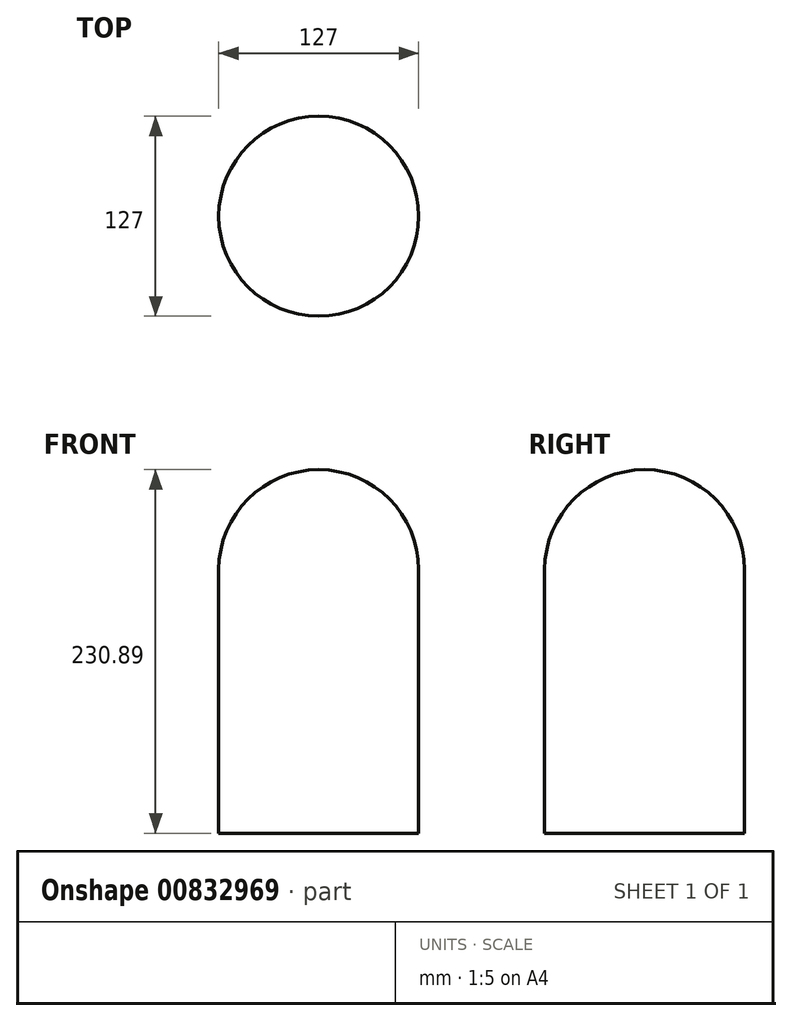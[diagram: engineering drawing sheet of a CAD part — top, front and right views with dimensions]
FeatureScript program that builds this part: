
annotation { "Feature Type Name" : "Feature", "Feature Type Description" : "" }
export const myFeature = defineFeature(function(context is Context, id is Id, definition is map)
    precondition{}
    {
        {
            var Q0;
            Q0=qCreatedBy(makeId("Top.planeOp"),FACE);
            var sketch = newSketch(context, id + "F0", { "sketchPlane" : qUnion([Q0])});
            skCircle(sketch, "E0", {"center": v(0, 0) * mm, "radius": 63.5 * mm});
            skSolve(sketch);
        }
        {
            var Q0;
            Q0 = qSketchRegion(id + "F0", true);
            extrude(context, id + "F1", {"entities" : qUnion([Q0]), "depth" : 167.39 * mm, "offsetDistance" : 25.4 * mm});
        }
        {
            var Q0;
            Q0=makeQuery(id+"F1.opExtrude","CAP_FACE",FACE,{"disambiguationData":[OSD([sQuery(id+"F0.wireOp",EDGE,"E0")])],"isStart":false});
            var sketch = newSketch(context, id + "F2", { "sketchPlane" : qUnion([Q0])});
            skLineSegment(sketch, "E1", {"start": v(0, 88.9) * mm, "end": v(0, -88.9) * mm});
            skArc(sketch, "E2", {"start": v(0, 88.9) * mm, "mid": v(88.9, 0) * mm, "end": v(0, -88.9) * mm});
            skSolve(sketch);
        }
        {
            var Q0;
            {var subQ0=sQuery(id+"F2.wireOp",EDGE,"E2");Q0=makeQuery(id+"F2.imprint","IMPRINT",FACE,{"disambiguationData":[TD([[makeQuery(id+"F2.imprint","IMPRINT",EDGE,{"derivedFrom":subQ0}),-1.0]])]});}
            var Q1;
            {var subQ0=sQuery(id+"F2.wireOp",EDGE,"E1");var subQ1=makeQuery(id+"F1.opExtrude","CAP_EDGE",EDGE,{"disambiguationData":[OSD([sQuery(id+"F0.wireOp",EDGE,"E0")])],"isStart":false});var subQ2=makeQuery(id+"F2.imprint","INTERSECT",VERTEX,{"disambiguationData":[OD(0.0)],"derivedFrom":[subQ1,subQ0]});Q1=makeQuery(id+"F2.imprint","IMPRINT",FACE,{"disambiguationData":[TD([[makeQuery(id+"F2.imprint","IMPRINT",EDGE,{"disambiguationData":[TD([[subQ2,-1.0]])],"derivedFrom":subQ0}),1.0]])]});}
            var Q2;
            Q2=sQuery(id+"F2.wireOp",EDGE,"E1");
            revolve(context, id + "F3", {"operationType" : NewBodyOperationType.ADD, "surfaceOperationType" : NewSurfaceOperationType.NEW, "entities" : qUnion([Q0, Q1]), "axis" : qUnion([Q2]), "revolveType" : RevolveType.ONE_DIRECTION, "angle" : 180 * degree});
        }
    });
